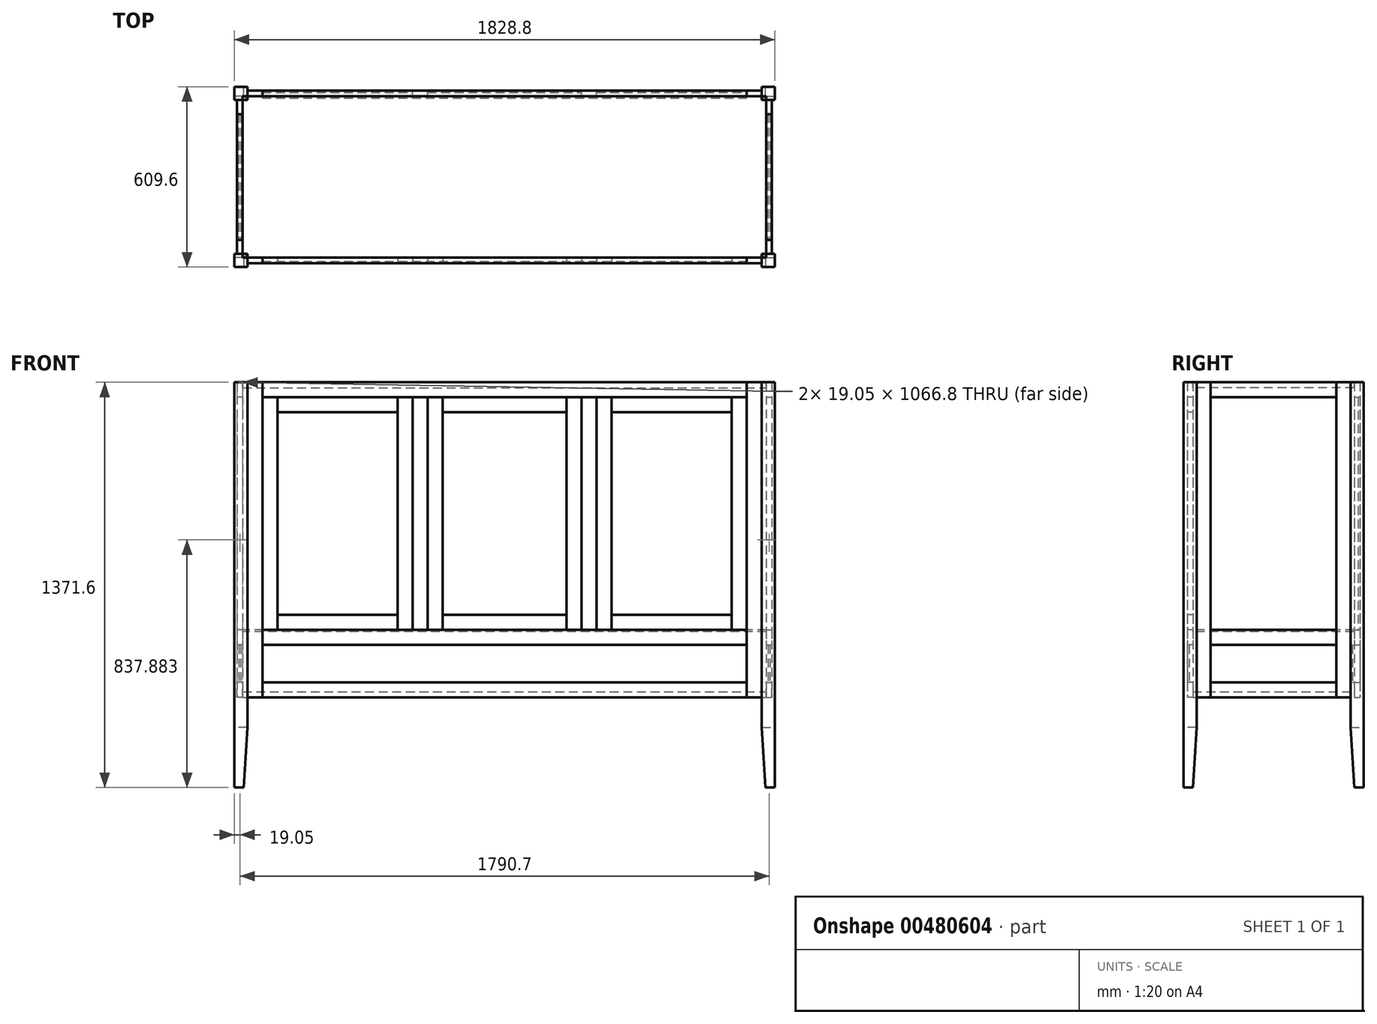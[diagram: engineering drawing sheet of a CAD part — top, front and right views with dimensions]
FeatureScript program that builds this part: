
annotation { "Feature Type Name" : "Feature", "Feature Type Description" : "" }
export const myFeature = defineFeature(function(context is Context, id is Id, definition is map)
    precondition{}
    {
        {
            var Q0;
            Q0=qCreatedBy(makeId("Front.planeOp"),FACE);
            var sketch = newSketch(context, id + "F0", { "sketchPlane" : qUnion([Q0])});
            skLineSegment(sketch, "E0.bottom", {"start": v(-628.95, 1371.6) * mm, "end": v(-584.5, 1371.6) * mm});
            skLineSegment(sketch, "E0.top", {"start": v(-628.95, 0) * mm, "end": v(-584.5, 0) * mm});
            skLineSegment(sketch, "E0.left", {"start": v(-628.95, 1371.6) * mm, "end": v(-628.95, 0) * mm});
            skLineSegment(sketch, "E0.right", {"start": v(-584.5, 1371.6) * mm, "end": v(-584.5, 0) * mm});
            skSolve(sketch);
        }
        {
            var Q0;
            Q0=qSketchRegion(id+"F0",true);
            extrude(context, id + "F1", {"entities" : qUnion([Q0]), "depth" : 44.45 * mm});
        }
        {
            var Q0;
            Q0=makeQuery(id+"F1.opExtrude","CAP_FACE",FACE,{"disambiguationData":[OSD([sQuery(id+"F0.wireOp",EDGE,"E0.bottom"),sQuery(id+"F0.wireOp",EDGE,"E0.top"),sQuery(id+"F0.wireOp",EDGE,"E0.left"),sQuery(id+"F0.wireOp",EDGE,"E0.right")])],"isStart":false});
            var sketch = newSketch(context, id + "F2", { "sketchPlane" : qUnion([Q0])});
            skPoint(sketch, "E1", {"position": v(-584.5, 203.2) * mm});
            skPoint(sketch, "E2", {"position": v(-597.2, 0) * mm});
            skLineSegment(sketch, "E3", {"start": v(-597.2, 0) * mm, "end": v(-584.5, 203.2) * mm});
            skLineSegment(sketch, "E4", {"start": v(-597.2, 0) * mm, "end": v(-584.5, 0) * mm});
            skLineSegment(sketch, "E5", {"start": v(-584.5, 0) * mm, "end": v(-584.5, 203.2) * mm});
            skSolve(sketch);
        }
        {
            var Q0;
            Q0=makeQuery(id+"F2.imprint","IMPRINT",FACE,{"disambiguationData":[TD([[makeQuery(id+"F2.imprint","IMPRINT",EDGE,{"derivedFrom":sQuery(id+"F2.wireOp",EDGE,"E3")}),-1.0]])]});
            extrude(context, id + "F3", {"entities" : qUnion([Q0]), "operationType" : NewBodyOperationType.REMOVE, "endBound" : BoundingType.THROUGH_ALL, "oppositeDirection" : true, "depth" : 25.4 * mm});
        }
        {
            var Q0;
            Q0=makeQuery(id+"F1.opExtrude","SWEPT_FACE",FACE,{"disambiguationData":[OSD([sQuery(id+"F0.wireOp",EDGE,"E0.left")])]});
            var sketch = newSketch(context, id + "F4", { "sketchPlane" : qUnion([Q0])});
            skPoint(sketch, "E6", {"position": v(0, 203.2) * mm});
            skPoint(sketch, "E7", {"position": v(12.7, 0) * mm});
            skLineSegment(sketch, "E8", {"start": v(0, 203.2) * mm, "end": v(12.7, 0) * mm});
            skLineSegment(sketch, "E9", {"start": v(0, 0) * mm, "end": v(0, 203.2) * mm});
            skSolve(sketch);
        }
        {
            var Q0;
            {var subQ0=sQuery(id+"F4.wireOp",EDGE,"E8");Q0=makeQuery(id+"F4.imprint","IMPRINT",FACE,{"disambiguationData":[TD([[makeQuery(id+"F4.imprint","IMPRINT",EDGE,{"derivedFrom":subQ0}),-1.0]])]});}
            extrude(context, id + "F5", {"entities" : qUnion([Q0]), "operationType" : NewBodyOperationType.REMOVE, "endBound" : BoundingType.THROUGH_ALL, "oppositeDirection" : true, "depth" : 25.4 * mm});
        }
        {
            var Q0;
            Q0=makeQuery(id+"F1.opExtrude","CAP_FACE",FACE,{"disambiguationData":[OSD([sQuery(id+"F0.wireOp",EDGE,"E0.bottom"),sQuery(id+"F0.wireOp",EDGE,"E0.top"),sQuery(id+"F0.wireOp",EDGE,"E0.left"),sQuery(id+"F0.wireOp",EDGE,"E0.right")])],"isStart":false});
            cPlane(context, id + "F6", {"entities" : qUnion([Q0]), "cplaneType" : CPlaneType.OFFSET, "offset" : 304.8 * mm, "oppositeDirection" : true, "width" : 152.4 * mm, "height" : 152.4 * mm});
        }
        {
            var Q0;
            Q0=makeQuery(id+"F1.opExtrude","SWEPT_FACE",FACE,{"disambiguationData":[OSD([sQuery(id+"F0.wireOp",EDGE,"E0.left")])]});
            cPlane(context, id + "F7", {"entities" : qUnion([Q0]), "cplaneType" : CPlaneType.OFFSET, "offset" : 9.52 * mm, "oppositeDirection" : true, "width" : 152.4 * mm, "height" : 152.4 * mm});
        }
        {
            var Q0;
            Q0=qCreatedBy(id+"F7.planeOp",FACE);
            var sketch = newSketch(context, id + "F8", { "sketchPlane" : qUnion([Q0])});
            skPoint(sketch, "E10", {"position": v(0, 1371.28) * mm});
            skPoint(sketch, "E11", {"position": v(0, 304.48) * mm});
            skLineSegment(sketch, "E12.bottom", {"start": v(0, 1371.28) * mm, "end": v(-47.62, 1371.28) * mm});
            skLineSegment(sketch, "E12.top", {"start": v(0, 304.48) * mm, "end": v(-47.62, 304.48) * mm});
            skLineSegment(sketch, "E12.left", {"start": v(0, 1371.28) * mm, "end": v(0, 304.48) * mm});
            skLineSegment(sketch, "E12.right", {"start": v(-47.62, 1371.28) * mm, "end": v(-47.62, 304.48) * mm});
            skSolve(sketch);
        }
        {
            var Q0;
            Q0=makeQuery(id+"F8.imprint","IMPRINT",FACE,{"disambiguationData":[TD([[makeQuery(id+"F8.imprint","IMPRINT",EDGE,{"derivedFrom":sQuery(id+"F8.wireOp",EDGE,"E12.bottom")}),1.0]])]});
            extrude(context, id + "F9", {"entities" : qUnion([Q0]), "operationType" : NewBodyOperationType.ADD, "oppositeDirection" : true, "depth" : 19.05 * mm});
        }
        {
            var Q0;
            Q0=makeQuery(id+"F1.opExtrude","SWEPT_BODY",BODY,{"disambiguationData":[OSD([sQuery(id+"F0.wireOp",EDGE,"E0.bottom"),sQuery(id+"F0.wireOp",EDGE,"E0.top"),sQuery(id+"F0.wireOp",EDGE,"E0.left"),sQuery(id+"F0.wireOp",EDGE,"E0.right")])]});
            var Q1;
            Q1=qCreatedBy(id+"F6.planeOp",FACE);
            mirror(context, id + "F10", {"entities" : qUnion([Q0]), "mirrorPlane" : qUnion([Q1])});
        }
        {
            var Q0;
            Q0=qCreatedBy(id+"F7.planeOp",FACE);
            var sketch = newSketch(context, id + "F11", { "sketchPlane" : qUnion([Q0])});
            skLineSegment(sketch, "E13.bottom", {"start": v(-473.08, 1371.28) * mm, "end": v(-47.62, 1371.28) * mm});
            skLineSegment(sketch, "E13.top", {"start": v(-473.08, 1320.48) * mm, "end": v(-47.62, 1320.48) * mm});
            skLineSegment(sketch, "E13.left", {"start": v(-473.08, 1371.28) * mm, "end": v(-473.08, 1320.48) * mm});
            skLineSegment(sketch, "E13.right", {"start": v(-47.62, 1371.28) * mm, "end": v(-47.62, 1320.48) * mm});
            skSolve(sketch);
        }
        {
            var Q0;
            Q0=makeQuery(id+"F11.imprint","IMPRINT",FACE,{"disambiguationData":[TD([[makeQuery(id+"F11.imprint","IMPRINT",EDGE,{"derivedFrom":sQuery(id+"F11.wireOp",EDGE,"E13.bottom")}),-1.0]])]});
            extrude(context, id + "F12", {"entities" : qUnion([Q0]), "oppositeDirection" : true, "depth" : 19.05 * mm});
        }
        {
            var Q0;
            Q0=qCreatedBy(id+"F7.planeOp",FACE);
            var sketch = newSketch(context, id + "F13", { "sketchPlane" : qUnion([Q0])});
            skLineSegment(sketch, "E14.bottom", {"start": v(-473.08, 304.48) * mm, "end": v(-47.62, 304.48) * mm});
            skLineSegment(sketch, "E14.top", {"start": v(-473.08, 355.28) * mm, "end": v(-47.62, 355.28) * mm});
            skLineSegment(sketch, "E14.left", {"start": v(-473.08, 304.48) * mm, "end": v(-473.08, 355.28) * mm});
            skLineSegment(sketch, "E14.right", {"start": v(-47.62, 304.48) * mm, "end": v(-47.62, 355.28) * mm});
            skSolve(sketch);
        }
        {
            var Q0;
            Q0=makeQuery(id+"F13.imprint","IMPRINT",FACE,{"disambiguationData":[TD([[makeQuery(id+"F13.imprint","IMPRINT",EDGE,{"derivedFrom":sQuery(id+"F13.wireOp",EDGE,"E14.bottom")}),1.0]])]});
            extrude(context, id + "F14", {"entities" : qUnion([Q0]), "oppositeDirection" : true, "depth" : 19.05 * mm});
        }
        {
            var Q0;
            Q0=qCreatedBy(id+"F7.planeOp",FACE);
            var sketch = newSketch(context, id + "F15", { "sketchPlane" : qUnion([Q0])});
            skPoint(sketch, "E15", {"position": v(-473.08, 1371.28) * mm});
            skPoint(sketch, "E16", {"position": v(-473.08, 533.08) * mm});
            skLineSegment(sketch, "E17.bottom", {"start": v(-473.08, 533.08) * mm, "end": v(-47.62, 533.08) * mm});
            skLineSegment(sketch, "E17.top", {"start": v(-473.08, 482.28) * mm, "end": v(-47.62, 482.28) * mm});
            skLineSegment(sketch, "E17.left", {"start": v(-473.08, 533.08) * mm, "end": v(-473.08, 482.28) * mm});
            skLineSegment(sketch, "E17.right", {"start": v(-47.62, 533.08) * mm, "end": v(-47.62, 482.28) * mm});
            skSolve(sketch);
        }
        {
            var Q0;
            Q0=makeQuery(id+"F15.imprint","IMPRINT",FACE,{"disambiguationData":[TD([[makeQuery(id+"F15.imprint","IMPRINT",EDGE,{"derivedFrom":sQuery(id+"F15.wireOp",EDGE,"E17.bottom")}),-1.0]])]});
            extrude(context, id + "F16", {"entities" : qUnion([Q0]), "oppositeDirection" : true, "depth" : 19.05 * mm});
        }
        {
            var Q0;
            Q0=makeQuery(id+"F16.opExtrude","CAP_FACE",FACE,{"disambiguationData":[OSD([sQuery(id+"F15.wireOp",EDGE,"E17.bottom"),sQuery(id+"F15.wireOp",EDGE,"E17.top"),sQuery(id+"F15.wireOp",EDGE,"E17.left"),sQuery(id+"F15.wireOp",EDGE,"E17.right")])],"isStart":true});
            cPlane(context, id + "F17", {"entities" : qUnion([Q0]), "cplaneType" : CPlaneType.OFFSET, "offset" : 6.35 * mm, "oppositeDirection" : true, "width" : 152.4 * mm, "height" : 152.4 * mm});
        }
        {
            var Q0;
            Q0=qCreatedBy(id+"F17.planeOp",FACE);
            var sketch = newSketch(context, id + "F18", { "sketchPlane" : qUnion([Q0])});
            skLineSegment(sketch, "E18.bottom", {"start": v(-473.08, 482.28) * mm, "end": v(-47.62, 482.28) * mm});
            skLineSegment(sketch, "E18.top", {"start": v(-473.08, 355.28) * mm, "end": v(-47.62, 355.28) * mm});
            skLineSegment(sketch, "E18.left", {"start": v(-473.08, 482.28) * mm, "end": v(-473.08, 355.28) * mm});
            skLineSegment(sketch, "E18.right", {"start": v(-47.62, 482.28) * mm, "end": v(-47.62, 355.28) * mm});
            skSolve(sketch);
        }
        {
            var Q0;
            Q0=makeQuery(id+"F18.imprint","IMPRINT",FACE,{"disambiguationData":[TD([[makeQuery(id+"F18.imprint","IMPRINT",EDGE,{"derivedFrom":sQuery(id+"F18.wireOp",EDGE,"E18.bottom")}),-1.0]])]});
            extrude(context, id + "F19", {"entities" : qUnion([Q0]), "oppositeDirection" : true, "depth" : 6.35 * mm});
        }
        {
            var Q0;
            Q0=makeQuery(id+"F1.opExtrude","SWEPT_FACE",FACE,{"disambiguationData":[OSD([sQuery(id+"F0.wireOp",EDGE,"E0.left")])]});
            cPlane(context, id + "F20", {"entities" : qUnion([Q0]), "cplaneType" : CPlaneType.OFFSET, "offset" : 914.4 * mm, "oppositeDirection" : true, "width" : 152.4 * mm, "height" : 152.4 * mm});
        }
        {
            var Q0;
            Q0=makeQuery(id+"F1.opExtrude","SWEPT_BODY",BODY,{"disambiguationData":[OSD([sQuery(id+"F0.wireOp",EDGE,"E0.bottom"),sQuery(id+"F0.wireOp",EDGE,"E0.top"),sQuery(id+"F0.wireOp",EDGE,"E0.left"),sQuery(id+"F0.wireOp",EDGE,"E0.right")])]});
            var Q1;
            Q1=makeQuery(id+"F14.opExtrude","SWEPT_BODY",BODY,{"disambiguationData":[OSD([sQuery(id+"F13.wireOp",EDGE,"E14.bottom"),sQuery(id+"F13.wireOp",EDGE,"E14.top"),sQuery(id+"F13.wireOp",EDGE,"E14.left"),sQuery(id+"F13.wireOp",EDGE,"E14.right")])]});
            var Q2;
            Q2=makeQuery(id+"F12.opExtrude","SWEPT_BODY",BODY,{"disambiguationData":[OSD([sQuery(id+"F11.wireOp",EDGE,"E13.bottom"),sQuery(id+"F11.wireOp",EDGE,"E13.top"),sQuery(id+"F11.wireOp",EDGE,"E13.left"),sQuery(id+"F11.wireOp",EDGE,"E13.right")])]});
            var Q3;
            Q3=makeQuery(id+"F10.opPattern","COPY",BODY,{"derivedFrom":makeQuery(id+"F1.opExtrude","SWEPT_BODY",BODY,{"disambiguationData":[OSD([sQuery(id+"F0.wireOp",EDGE,"E0.bottom"),sQuery(id+"F0.wireOp",EDGE,"E0.top"),sQuery(id+"F0.wireOp",EDGE,"E0.left"),sQuery(id+"F0.wireOp",EDGE,"E0.right")])]}),"instanceName":"1"});
            var Q4;
            Q4=makeQuery(id+"F16.opExtrude","SWEPT_BODY",BODY,{"disambiguationData":[OSD([sQuery(id+"F15.wireOp",EDGE,"E17.bottom"),sQuery(id+"F15.wireOp",EDGE,"E17.top"),sQuery(id+"F15.wireOp",EDGE,"E17.left"),sQuery(id+"F15.wireOp",EDGE,"E17.right")])]});
            var Q5;
            Q5=makeQuery(id+"F19.opExtrude","SWEPT_BODY",BODY,{"disambiguationData":[OSD([sQuery(id+"F18.wireOp",EDGE,"E18.bottom"),sQuery(id+"F18.wireOp",EDGE,"E18.top"),sQuery(id+"F18.wireOp",EDGE,"E18.left"),sQuery(id+"F18.wireOp",EDGE,"E18.right")])]});
            var Q6;
            Q6=qCreatedBy(id+"F20.planeOp",FACE);
            mirror(context, id + "F21", {"entities" : qUnion([Q0, Q1, Q2, Q3, Q4, Q5]), "mirrorPlane" : qUnion([Q6])});
        }
        {
            var Q0;
            Q0=makeQuery(id+"F21.opPattern","COPY",FACE,{"derivedFrom":makeQuery(id+"F1.opExtrude","CAP_FACE",FACE,{"disambiguationData":[OSD([sQuery(id+"F0.wireOp",EDGE,"E0.bottom"),sQuery(id+"F0.wireOp",EDGE,"E0.top"),sQuery(id+"F0.wireOp",EDGE,"E0.left"),sQuery(id+"F0.wireOp",EDGE,"E0.right")])],"isStart":false}),"instanceName":"1"});
            cPlane(context, id + "F22", {"entities" : qUnion([Q0]), "cplaneType" : CPlaneType.OFFSET, "offset" : 12.7 * mm, "oppositeDirection" : true, "width" : 152.4 * mm, "height" : 152.4 * mm});
        }
        {
            var Q0;
            Q0=qCreatedBy(id+"F22.planeOp",FACE);
            var sketch = newSketch(context, id + "F23", { "sketchPlane" : qUnion([Q0])});
            skLineSegment(sketch, "E19.bottom", {"start": v(-584.5, 1371.6) * mm, "end": v(-533.7, 1371.6) * mm});
            skLineSegment(sketch, "E19.top", {"start": v(-584.5, 304.48) * mm, "end": v(-533.7, 304.48) * mm});
            skLineSegment(sketch, "E19.left", {"start": v(-584.5, 1371.6) * mm, "end": v(-584.5, 304.48) * mm});
            skLineSegment(sketch, "E19.right", {"start": v(-533.7, 1371.6) * mm, "end": v(-533.7, 304.48) * mm});
            skSolve(sketch);
        }
        {
            var Q0;
            Q0=qSketchRegion(id+"F23",true);
            extrude(context, id + "F24", {"entities" : qUnion([Q0]), "oppositeDirection" : true, "depth" : 19.05 * mm});
        }
        {
            var Q0;
            Q0=qCreatedBy(id+"F22.planeOp",FACE);
            var sketch = newSketch(context, id + "F25", { "sketchPlane" : qUnion([Q0])});
            skLineSegment(sketch, "E20.bottom", {"start": v(-533.7, 1371.6) * mm, "end": v(1104.6, 1371.6) * mm});
            skLineSegment(sketch, "E20.top", {"start": v(-533.7, 1320.8) * mm, "end": v(1104.6, 1320.8) * mm});
            skLineSegment(sketch, "E20.left", {"start": v(-533.7, 1371.6) * mm, "end": v(-533.7, 1320.8) * mm});
            skLineSegment(sketch, "E20.right", {"start": v(1104.6, 1371.6) * mm, "end": v(1104.6, 1320.8) * mm});
            skSolve(sketch);
        }
        {
            var Q0;
            Q0=qSketchRegion(id+"F25",true);
            extrude(context, id + "F26", {"entities" : qUnion([Q0]), "oppositeDirection" : true, "depth" : 19.05 * mm});
        }
        {
            var Q0;
            Q0=makeQuery(id+"F24.opExtrude","SWEPT_BODY",BODY,{"disambiguationData":[OSD([sQuery(id+"F23.wireOp",EDGE,"E19.bottom"),sQuery(id+"F23.wireOp",EDGE,"E19.top"),sQuery(id+"F23.wireOp",EDGE,"E19.left"),sQuery(id+"F23.wireOp",EDGE,"E19.right")])]});
            var Q1;
            Q1=qCreatedBy(id+"F20.planeOp",FACE);
            mirror(context, id + "F27", {"entities" : qUnion([Q0]), "mirrorPlane" : qUnion([Q1])});
        }
        {
            var Q0;
            Q0=qCreatedBy(id+"F22.planeOp",FACE);
            var sketch = newSketch(context, id + "F28", { "sketchPlane" : qUnion([Q0])});
            skLineSegment(sketch, "E21.bottom", {"start": v(-533.7, 355.28) * mm, "end": v(1104.6, 355.28) * mm});
            skLineSegment(sketch, "E21.top", {"start": v(-533.7, 304.48) * mm, "end": v(1104.6, 304.48) * mm});
            skLineSegment(sketch, "E21.left", {"start": v(-533.7, 355.28) * mm, "end": v(-533.7, 304.48) * mm});
            skLineSegment(sketch, "E21.right", {"start": v(1104.6, 355.28) * mm, "end": v(1104.6, 304.48) * mm});
            skSolve(sketch);
        }
        {
            var Q0;
            Q0=qSketchRegion(id+"F28",true);
            extrude(context, id + "F29", {"entities" : qUnion([Q0]), "oppositeDirection" : true, "depth" : 19.05 * mm});
        }
        {
            var Q0;
            Q0=qCreatedBy(id+"F22.planeOp",FACE);
            var sketch = newSketch(context, id + "F30", { "sketchPlane" : qUnion([Q0])});
            skLineSegment(sketch, "E22.bottom", {"start": v(-533.7, 533.08) * mm, "end": v(1104.6, 533.08) * mm});
            skLineSegment(sketch, "E22.top", {"start": v(-533.7, 482.28) * mm, "end": v(1104.6, 482.28) * mm});
            skLineSegment(sketch, "E22.left", {"start": v(-533.7, 533.08) * mm, "end": v(-533.7, 482.28) * mm});
            skLineSegment(sketch, "E22.right", {"start": v(1104.6, 533.08) * mm, "end": v(1104.6, 482.28) * mm});
            skSolve(sketch);
        }
        {
            var Q0;
            Q0=qSketchRegion(id+"F30",true);
            extrude(context, id + "F31", {"entities" : qUnion([Q0]), "oppositeDirection" : true, "depth" : 19.05 * mm});
        }
        {
            var Q0;
            Q0=qCreatedBy(id+"F22.planeOp",FACE);
            var sketch = newSketch(context, id + "F32", { "sketchPlane" : qUnion([Q0])});
            skLineSegment(sketch, "E23.bottom", {"start": v(-25.7, 1320.8) * mm, "end": v(25.1, 1320.8) * mm});
            skLineSegment(sketch, "E23.top", {"start": v(-25.7, 533.08) * mm, "end": v(25.1, 533.08) * mm});
            skLineSegment(sketch, "E23.left", {"start": v(-25.7, 1320.8) * mm, "end": v(-25.7, 533.08) * mm});
            skLineSegment(sketch, "E23.right", {"start": v(25.1, 1320.8) * mm, "end": v(25.1, 533.08) * mm});
            skSolve(sketch);
        }
        {
            var Q0;
            Q0=qSketchRegion(id+"F32",true);
            extrude(context, id + "F33", {"entities" : qUnion([Q0]), "oppositeDirection" : true, "depth" : 19.05 * mm});
        }
        {
            var Q0;
            Q0=makeQuery(id+"F33.opExtrude","SWEPT_BODY",BODY,{"disambiguationData":[OSD([sQuery(id+"F32.wireOp",EDGE,"E23.bottom"),sQuery(id+"F32.wireOp",EDGE,"E23.top"),sQuery(id+"F32.wireOp",EDGE,"E23.left"),sQuery(id+"F32.wireOp",EDGE,"E23.right")])]});
            var Q1;
            Q1=makeQuery(id+"FRYgR2zi93UsPrp_9.opExtrude","SWEPT_BODY",BODY,{"disambiguationData":[OSD([sQuery(id+"FfaSuB3CfZjcmVR_9.wireOp",EDGE,"jGVs514A-PyTt-ZbNQ-JDFk-VF9dIN6a2kFS.bottom"),sQuery(id+"FfaSuB3CfZjcmVR_9.wireOp",EDGE,"jGVs514A-PyTt-ZbNQ-JDFk-VF9dIN6a2kFS.top"),sQuery(id+"FfaSuB3CfZjcmVR_9.wireOp",EDGE,"jGVs514A-PyTt-ZbNQ-JDFk-VF9dIN6a2kFS.left"),sQuery(id+"FfaSuB3CfZjcmVR_9.wireOp",EDGE,"jGVs514A-PyTt-ZbNQ-JDFk-VF9dIN6a2kFS.right")])]});
            var Q2;
            Q2=qCreatedBy(id+"F20.planeOp",FACE);
            mirror(context, id + "F34", {"entities" : qUnion([Q0, Q1]), "mirrorPlane" : qUnion([Q2])});
        }
        {
            var Q0;
            Q0=makeQuery(id+"F24.opExtrude","SWEPT_BODY",BODY,{"disambiguationData":[OSD([sQuery(id+"F23.wireOp",EDGE,"E19.bottom"),sQuery(id+"F23.wireOp",EDGE,"E19.top"),sQuery(id+"F23.wireOp",EDGE,"E19.left"),sQuery(id+"F23.wireOp",EDGE,"E19.right")])]});
            var Q1;
            Q1=makeQuery(id+"F26.opExtrude","SWEPT_BODY",BODY,{"disambiguationData":[OSD([sQuery(id+"F25.wireOp",EDGE,"E20.bottom"),sQuery(id+"F25.wireOp",EDGE,"E20.top"),sQuery(id+"F25.wireOp",EDGE,"E20.left"),sQuery(id+"F25.wireOp",EDGE,"E20.right")])]});
            var Q2;
            Q2=makeQuery(id+"F33.opExtrude","SWEPT_BODY",BODY,{"disambiguationData":[OSD([sQuery(id+"F32.wireOp",EDGE,"E23.bottom"),sQuery(id+"F32.wireOp",EDGE,"E23.top"),sQuery(id+"F32.wireOp",EDGE,"E23.left"),sQuery(id+"F32.wireOp",EDGE,"E23.right")])]});
            var Q3;
            Q3=makeQuery(id+"F34.opPattern","COPY",BODY,{"derivedFrom":makeQuery(id+"F33.opExtrude","SWEPT_BODY",BODY,{"disambiguationData":[OSD([sQuery(id+"F32.wireOp",EDGE,"E23.bottom"),sQuery(id+"F32.wireOp",EDGE,"E23.top"),sQuery(id+"F32.wireOp",EDGE,"E23.left"),sQuery(id+"F32.wireOp",EDGE,"E23.right")])]}),"instanceName":"1"});
            var Q4;
            Q4=makeQuery(id+"F27.opPattern","COPY",BODY,{"derivedFrom":makeQuery(id+"F24.opExtrude","SWEPT_BODY",BODY,{"disambiguationData":[OSD([sQuery(id+"F23.wireOp",EDGE,"E19.bottom"),sQuery(id+"F23.wireOp",EDGE,"E19.top"),sQuery(id+"F23.wireOp",EDGE,"E19.left"),sQuery(id+"F23.wireOp",EDGE,"E19.right")])]}),"instanceName":"1"});
            var Q5;
            Q5=makeQuery(id+"F31.opExtrude","SWEPT_BODY",BODY,{"disambiguationData":[OSD([sQuery(id+"F30.wireOp",EDGE,"E22.bottom"),sQuery(id+"F30.wireOp",EDGE,"E22.top"),sQuery(id+"F30.wireOp",EDGE,"E22.left"),sQuery(id+"F30.wireOp",EDGE,"E22.right")])]});
            var Q6;
            Q6=makeQuery(id+"F29.opExtrude","SWEPT_BODY",BODY,{"disambiguationData":[OSD([sQuery(id+"F28.wireOp",EDGE,"E21.bottom"),sQuery(id+"F28.wireOp",EDGE,"E21.top"),sQuery(id+"F28.wireOp",EDGE,"E21.left"),sQuery(id+"F28.wireOp",EDGE,"E21.right")])]});
            var Q7;
            Q7=makeQuery(id+"F34.opPattern","COPY",BODY,{"derivedFrom":makeQuery(id+"FRYgR2zi93UsPrp_9.opExtrude","SWEPT_BODY",BODY,{"disambiguationData":[OSD([sQuery(id+"FfaSuB3CfZjcmVR_9.wireOp",EDGE,"jGVs514A-PyTt-ZbNQ-JDFk-VF9dIN6a2kFS.bottom"),sQuery(id+"FfaSuB3CfZjcmVR_9.wireOp",EDGE,"jGVs514A-PyTt-ZbNQ-JDFk-VF9dIN6a2kFS.top"),sQuery(id+"FfaSuB3CfZjcmVR_9.wireOp",EDGE,"jGVs514A-PyTt-ZbNQ-JDFk-VF9dIN6a2kFS.left"),sQuery(id+"FfaSuB3CfZjcmVR_9.wireOp",EDGE,"jGVs514A-PyTt-ZbNQ-JDFk-VF9dIN6a2kFS.right")])]}),"instanceName":"1"});
            var Q8;
            Q8=makeQuery(id+"FRYgR2zi93UsPrp_9.opExtrude","SWEPT_BODY",BODY,{"disambiguationData":[OSD([sQuery(id+"FfaSuB3CfZjcmVR_9.wireOp",EDGE,"jGVs514A-PyTt-ZbNQ-JDFk-VF9dIN6a2kFS.bottom"),sQuery(id+"FfaSuB3CfZjcmVR_9.wireOp",EDGE,"jGVs514A-PyTt-ZbNQ-JDFk-VF9dIN6a2kFS.top"),sQuery(id+"FfaSuB3CfZjcmVR_9.wireOp",EDGE,"jGVs514A-PyTt-ZbNQ-JDFk-VF9dIN6a2kFS.left"),sQuery(id+"FfaSuB3CfZjcmVR_9.wireOp",EDGE,"jGVs514A-PyTt-ZbNQ-JDFk-VF9dIN6a2kFS.right")])]});
            var Q9;
            Q9=makeQuery(id+"FIeeD6PPRITTbVt_10.opExtrude","SWEPT_BODY",BODY,{"disambiguationData":[OSD([sQuery(id+"FnYbJkNIQu2NAMf_10.wireOp",EDGE,"rAF0CF05-2Poy-62uF-igAy-b5mA2g4RPxVq.bottom"),sQuery(id+"FnYbJkNIQu2NAMf_10.wireOp",EDGE,"rAF0CF05-2Poy-62uF-igAy-b5mA2g4RPxVq.top"),sQuery(id+"FnYbJkNIQu2NAMf_10.wireOp",EDGE,"rAF0CF05-2Poy-62uF-igAy-b5mA2g4RPxVq.left"),sQuery(id+"FnYbJkNIQu2NAMf_10.wireOp",EDGE,"rAF0CF05-2Poy-62uF-igAy-b5mA2g4RPxVq.right")])]});
            var Q10;
            Q10=makeQuery(id+"FIeeD6PPRITTbVt_10.opExtrude","SWEPT_BODY",BODY,{"disambiguationData":[OSD([sQuery(id+"FnYbJkNIQu2NAMf_10.wireOp",EDGE,"fFBXAJHD-Mimp-aTbj-Gqx7-02bonivjZSQP.bottom"),sQuery(id+"FnYbJkNIQu2NAMf_10.wireOp",EDGE,"fFBXAJHD-Mimp-aTbj-Gqx7-02bonivjZSQP.top"),sQuery(id+"FnYbJkNIQu2NAMf_10.wireOp",EDGE,"fFBXAJHD-Mimp-aTbj-Gqx7-02bonivjZSQP.left"),sQuery(id+"FnYbJkNIQu2NAMf_10.wireOp",EDGE,"fFBXAJHD-Mimp-aTbj-Gqx7-02bonivjZSQP.right")])]});
            var Q11;
            Q11=makeQuery(id+"FIeeD6PPRITTbVt_10.opExtrude","SWEPT_BODY",BODY,{"disambiguationData":[OSD([sQuery(id+"FnYbJkNIQu2NAMf_10.wireOp",EDGE,"xDAJZFGa-3O6M-nzbW-7IkL-r6EZniyfeXkM.bottom"),sQuery(id+"FnYbJkNIQu2NAMf_10.wireOp",EDGE,"xDAJZFGa-3O6M-nzbW-7IkL-r6EZniyfeXkM.top"),sQuery(id+"FnYbJkNIQu2NAMf_10.wireOp",EDGE,"xDAJZFGa-3O6M-nzbW-7IkL-r6EZniyfeXkM.left"),sQuery(id+"FnYbJkNIQu2NAMf_10.wireOp",EDGE,"xDAJZFGa-3O6M-nzbW-7IkL-r6EZniyfeXkM.right")])]});
            var Q12;
            Q12=qCreatedBy(id+"F6.planeOp",FACE);
            mirror(context, id + "F35", {"entities" : qUnion([Q0, Q1, Q2, Q3, Q4, Q5, Q6, Q7, Q8, Q9, Q10, Q11]), "mirrorPlane" : qUnion([Q12])});
        }
        {
            var Q0;
            Q0=qCreatedBy(id+"F22.planeOp",FACE);
            var sketch = newSketch(context, id + "F36", { "sketchPlane" : qUnion([Q0])});
            skLineSegment(sketch, "E24.bottom", {"start": v(-533.7, 1320.8) * mm, "end": v(-482.9, 1320.8) * mm});
            skLineSegment(sketch, "E24.top", {"start": v(-533.7, 533.08) * mm, "end": v(-482.9, 533.08) * mm});
            skLineSegment(sketch, "E24.left", {"start": v(-533.7, 1320.8) * mm, "end": v(-533.7, 533.08) * mm});
            skLineSegment(sketch, "E24.right", {"start": v(-482.9, 1320.8) * mm, "end": v(-482.9, 533.08) * mm});
            skSolve(sketch);
        }
        {
            var Q0;
            Q0=qSketchRegion(id+"F36",true);
            extrude(context, id + "F37", {"entities" : qUnion([Q0]), "oppositeDirection" : true, "depth" : 19.05 * mm});
        }
        {
            var Q0;
            Q0=qCreatedBy(id+"F22.planeOp",FACE);
            var sketch = newSketch(context, id + "F38", { "sketchPlane" : qUnion([Q0])});
            skLineSegment(sketch, "E25.bottom", {"start": v(-76.5, 1320.8) * mm, "end": v(-25.7, 1320.8) * mm});
            skLineSegment(sketch, "E25.top", {"start": v(-76.5, 533.08) * mm, "end": v(-25.7, 533.08) * mm});
            skLineSegment(sketch, "E25.left", {"start": v(-76.5, 1320.8) * mm, "end": v(-76.5, 533.08) * mm});
            skLineSegment(sketch, "E25.right", {"start": v(-25.7, 1320.8) * mm, "end": v(-25.7, 533.08) * mm});
            skSolve(sketch);
        }
        {
            var Q0;
            Q0=qSketchRegion(id+"F38",true);
            extrude(context, id + "F39", {"entities" : qUnion([Q0]), "oppositeDirection" : true, "depth" : 19.05 * mm});
        }
        {
            var Q0;
            Q0=qCreatedBy(id+"F22.planeOp",FACE);
            var sketch = newSketch(context, id + "F40", { "sketchPlane" : qUnion([Q0])});
            skLineSegment(sketch, "E26.bottom", {"start": v(-482.9, 1320.8) * mm, "end": v(-76.5, 1320.8) * mm});
            skLineSegment(sketch, "E26.top", {"start": v(-482.9, 1270) * mm, "end": v(-76.5, 1270) * mm});
            skLineSegment(sketch, "E26.left", {"start": v(-482.9, 1320.8) * mm, "end": v(-482.9, 1270) * mm});
            skLineSegment(sketch, "E26.right", {"start": v(-76.5, 1320.8) * mm, "end": v(-76.5, 1270) * mm});
            skSolve(sketch);
        }
        {
            var Q0;
            Q0=qSketchRegion(id+"F40",true);
            extrude(context, id + "F41", {"entities" : qUnion([Q0]), "oppositeDirection" : true, "depth" : 19.05 * mm});
        }
        {
            var Q0;
            Q0=qCreatedBy(id+"F22.planeOp",FACE);
            var sketch = newSketch(context, id + "F42", { "sketchPlane" : qUnion([Q0])});
            skLineSegment(sketch, "E27.bottom", {"start": v(-482.9, 583.88) * mm, "end": v(-76.5, 583.88) * mm});
            skLineSegment(sketch, "E27.top", {"start": v(-482.9, 533.08) * mm, "end": v(-76.5, 533.08) * mm});
            skLineSegment(sketch, "E27.left", {"start": v(-482.9, 583.88) * mm, "end": v(-482.9, 533.08) * mm});
            skLineSegment(sketch, "E27.right", {"start": v(-76.5, 583.88) * mm, "end": v(-76.5, 533.08) * mm});
            skSolve(sketch);
        }
        {
            var Q0;
            Q0=qSketchRegion(id+"F42",true);
            extrude(context, id + "F43", {"entities" : qUnion([Q0]), "oppositeDirection" : true, "depth" : 19.05 * mm});
        }
        {
            var Q0;
            Q0=makeQuery(id+"F37.opExtrude","SWEPT_BODY",BODY,{"disambiguationData":[OSD([sQuery(id+"F36.wireOp",EDGE,"E24.bottom"),sQuery(id+"F36.wireOp",EDGE,"E24.top"),sQuery(id+"F36.wireOp",EDGE,"E24.left"),sQuery(id+"F36.wireOp",EDGE,"E24.right")])]});
            var Q1;
            Q1=makeQuery(id+"F41.opExtrude","SWEPT_BODY",BODY,{"disambiguationData":[OSD([sQuery(id+"F40.wireOp",EDGE,"E26.bottom"),sQuery(id+"F40.wireOp",EDGE,"E26.top"),sQuery(id+"F40.wireOp",EDGE,"E26.left"),sQuery(id+"F40.wireOp",EDGE,"E26.right")])]});
            var Q2;
            Q2=makeQuery(id+"F39.opExtrude","SWEPT_BODY",BODY,{"disambiguationData":[OSD([sQuery(id+"F38.wireOp",EDGE,"E25.bottom"),sQuery(id+"F38.wireOp",EDGE,"E25.top"),sQuery(id+"F38.wireOp",EDGE,"E25.left"),sQuery(id+"F38.wireOp",EDGE,"E25.right")])]});
            var Q3;
            Q3=makeQuery(id+"F43.opExtrude","SWEPT_BODY",BODY,{"disambiguationData":[OSD([sQuery(id+"F42.wireOp",EDGE,"E27.bottom"),sQuery(id+"F42.wireOp",EDGE,"E27.top"),sQuery(id+"F42.wireOp",EDGE,"E27.left"),sQuery(id+"F42.wireOp",EDGE,"E27.right")])]});
            var Q4;
            Q4=qCreatedBy(id+"F20.planeOp",FACE);
            mirror(context, id + "F44", {"entities" : qUnion([Q0, Q1, Q2, Q3]), "mirrorPlane" : qUnion([Q4])});
        }
        {
            var Q0;
            Q0=qCreatedBy(id+"F22.planeOp",FACE);
            var sketch = newSketch(context, id + "F45", { "sketchPlane" : qUnion([Q0])});
            skLineSegment(sketch, "E28.bottom", {"start": v(25.1, 1320.8) * mm, "end": v(75.9, 1320.8) * mm});
            skLineSegment(sketch, "E28.top", {"start": v(25.1, 533.08) * mm, "end": v(75.9, 533.08) * mm});
            skLineSegment(sketch, "E28.left", {"start": v(25.1, 1320.8) * mm, "end": v(25.1, 533.08) * mm});
            skLineSegment(sketch, "E28.right", {"start": v(75.9, 1320.8) * mm, "end": v(75.9, 533.08) * mm});
            skSolve(sketch);
        }
        {
            var Q0;
            Q0=qSketchRegion(id+"F45",true);
            extrude(context, id + "F46", {"entities" : qUnion([Q0]), "oppositeDirection" : true, "depth" : 19.05 * mm});
        }
        {
            var Q0;
            Q0=qCreatedBy(id+"F22.planeOp",FACE);
            var sketch = newSketch(context, id + "F47", { "sketchPlane" : qUnion([Q0])});
            skLineSegment(sketch, "E29.bottom", {"start": v(495, 1320.8) * mm, "end": v(545.8, 1320.8) * mm});
            skLineSegment(sketch, "E29.top", {"start": v(495, 533.08) * mm, "end": v(545.8, 533.08) * mm});
            skLineSegment(sketch, "E29.left", {"start": v(495, 1320.8) * mm, "end": v(495, 533.08) * mm});
            skLineSegment(sketch, "E29.right", {"start": v(545.8, 1320.8) * mm, "end": v(545.8, 533.08) * mm});
            skSolve(sketch);
        }
        {
            var Q0;
            Q0=qSketchRegion(id+"F47",true);
            extrude(context, id + "F48", {"entities" : qUnion([Q0]), "oppositeDirection" : true, "depth" : 19.05 * mm});
        }
        {
            var Q0;
            Q0=qCreatedBy(id+"F22.planeOp",FACE);
            var sketch = newSketch(context, id + "F49", { "sketchPlane" : qUnion([Q0])});
            skLineSegment(sketch, "E30.bottom", {"start": v(75.9, 1320.8) * mm, "end": v(495, 1320.8) * mm});
            skLineSegment(sketch, "E30.top", {"start": v(75.9, 1270) * mm, "end": v(495, 1270) * mm});
            skLineSegment(sketch, "E30.left", {"start": v(75.9, 1320.8) * mm, "end": v(75.9, 1270) * mm});
            skLineSegment(sketch, "E30.right", {"start": v(495, 1320.8) * mm, "end": v(495, 1270) * mm});
            skSolve(sketch);
        }
        {
            var Q0;
            Q0=qSketchRegion(id+"F49",true);
            extrude(context, id + "F50", {"entities" : qUnion([Q0]), "oppositeDirection" : true, "depth" : 19.05 * mm});
        }
        {
            var Q0;
            Q0=qCreatedBy(id+"F22.planeOp",FACE);
            var sketch = newSketch(context, id + "F51", { "sketchPlane" : qUnion([Q0])});
            skLineSegment(sketch, "E31.bottom", {"start": v(75.9, 583.88) * mm, "end": v(495, 583.88) * mm});
            skLineSegment(sketch, "E31.top", {"start": v(75.9, 533.08) * mm, "end": v(495, 533.08) * mm});
            skLineSegment(sketch, "E31.left", {"start": v(75.9, 583.88) * mm, "end": v(75.9, 533.08) * mm});
            skLineSegment(sketch, "E31.right", {"start": v(495, 583.88) * mm, "end": v(495, 533.08) * mm});
            skSolve(sketch);
        }
        {
            var Q0;
            Q0=qSketchRegion(id+"F51",true);
            extrude(context, id + "F52", {"entities" : qUnion([Q0]), "oppositeDirection" : true, "depth" : 19.05 * mm});
        }
        {
            var Q0;
            Q0=makeQuery(id+"F10.opPattern","COPY",FACE,{"derivedFrom":makeQuery(id+"F1.opExtrude","SWEPT_FACE",FACE,{"disambiguationData":[OSD([sQuery(id+"F0.wireOp",EDGE,"E0.bottom")])]}),"instanceName":"1"});
            var sketch = newSketch(context, id + "F53", { "sketchPlane" : qUnion([Q0])});
            skLineSegment(sketch, "E32.bottom", {"start": v(-600.37, 533.4) * mm, "end": v(1171.28, 533.4) * mm});
            skLineSegment(sketch, "E32.top", {"start": v(-600.37, -12.7) * mm, "end": v(1171.28, -12.7) * mm});
            skLineSegment(sketch, "E32.left", {"start": v(-600.37, 533.4) * mm, "end": v(-600.37, -12.7) * mm});
            skLineSegment(sketch, "E32.right", {"start": v(1171.28, 533.4) * mm, "end": v(1171.28, -12.7) * mm});
            skSolve(sketch);
        }
        {
            var Q0;
            Q0=qSketchRegion(id+"F53",true);
            extrude(context, id + "F54", {"entities" : qUnion([Q0]), "oppositeDirection" : true, "depth" : 19.05 * mm});
        }
        {
            var Q0;
            Q0=makeQuery(id+"F29.opExtrude","SWEPT_FACE",FACE,{"disambiguationData":[OSD([sQuery(id+"F28.wireOp",EDGE,"E21.top")])]});
            var sketch = newSketch(context, id + "F55", { "sketchPlane" : qUnion([Q0])});
            skLineSegment(sketch, "E33.bottom", {"start": v(-600.37, 12.7) * mm, "end": v(1171.28, 12.7) * mm});
            skLineSegment(sketch, "E33.top", {"start": v(-600.37, -533.4) * mm, "end": v(1171.28, -533.4) * mm});
            skLineSegment(sketch, "E33.left", {"start": v(-600.37, 12.7) * mm, "end": v(-600.37, -533.4) * mm});
            skLineSegment(sketch, "E33.right", {"start": v(1171.28, 12.7) * mm, "end": v(1171.28, -533.4) * mm});
            skSolve(sketch);
        }
        {
            var Q0;
            Q0=qSketchRegion(id+"F55",true);
            extrude(context, id + "F56", {"entities" : qUnion([Q0]), "oppositeDirection" : true, "depth" : 19.05 * mm});
        }
        {
            var Q0;
            Q0=makeQuery(id+"F31.opExtrude","CAP_FACE",FACE,{"disambiguationData":[OSD([sQuery(id+"F30.wireOp",EDGE,"E22.bottom"),sQuery(id+"F30.wireOp",EDGE,"E22.top"),sQuery(id+"F30.wireOp",EDGE,"E22.left"),sQuery(id+"F30.wireOp",EDGE,"E22.right")])],"isStart":true});
            var sketch = newSketch(context, id + "F57", { "sketchPlane" : qUnion([Q0])});
            skLineSegment(sketch, "E34.bottom", {"start": v(-533.7, 482.28) * mm, "end": v(1104.6, 482.28) * mm});
            skLineSegment(sketch, "E34.top", {"start": v(-533.7, 355.28) * mm, "end": v(1104.6, 355.28) * mm});
            skLineSegment(sketch, "E34.left", {"start": v(-533.7, 482.28) * mm, "end": v(-533.7, 355.28) * mm});
            skLineSegment(sketch, "E34.right", {"start": v(1104.6, 482.28) * mm, "end": v(1104.6, 355.28) * mm});
            skSolve(sketch);
        }
        {
            var Q0;
            Q0 = qSketchRegion(id + "F57", true);
            extrude(context, id + "F58", {"entities" : qUnion([Q0]), "oppositeDirection" : true, "depth" : 6.35 * mm});
        }
        {
            var Q0;
            Q0=makeQuery(id+"F35.opPattern","COPY",FACE,{"derivedFrom":makeQuery(id+"F31.opExtrude","CAP_FACE",FACE,{"disambiguationData":[OSD([sQuery(id+"F30.wireOp",EDGE,"E22.bottom"),sQuery(id+"F30.wireOp",EDGE,"E22.top"),sQuery(id+"F30.wireOp",EDGE,"E22.left"),sQuery(id+"F30.wireOp",EDGE,"E22.right")])],"isStart":true}),"instanceName":"1"});
            var sketch = newSketch(context, id + "F59", { "sketchPlane" : qUnion([Q0])});
            skLineSegment(sketch, "E35.bottom", {"start": v(-1104.6, 482.28) * mm, "end": v(533.7, 482.28) * mm});
            skLineSegment(sketch, "E35.top", {"start": v(-1104.6, 355.28) * mm, "end": v(533.7, 355.28) * mm});
            skLineSegment(sketch, "E35.left", {"start": v(-1104.6, 482.28) * mm, "end": v(-1104.6, 355.28) * mm});
            skLineSegment(sketch, "E35.right", {"start": v(533.7, 482.28) * mm, "end": v(533.7, 355.28) * mm});
            skSolve(sketch);
        }
        {
            var Q0;
            Q0 = qSketchRegion(id + "F59", true);
            extrude(context, id + "F60", {"entities" : qUnion([Q0]), "oppositeDirection" : true, "depth" : 25.4 * mm});
        }
        {
            var Q0;
            Q0=makeQuery(id+"F35.opPattern","COPY",FACE,{"derivedFrom":makeQuery(id+"F26.opExtrude","CAP_FACE",FACE,{"disambiguationData":[OSD([sQuery(id+"F25.wireOp",EDGE,"E20.bottom"),sQuery(id+"F25.wireOp",EDGE,"E20.top"),sQuery(id+"F25.wireOp",EDGE,"E20.left"),sQuery(id+"F25.wireOp",EDGE,"E20.right")])],"isStart":true}),"instanceName":"1"});
            var sketch = newSketch(context, id + "F61", { "sketchPlane" : qUnion([Q0])});
            skLineSegment(sketch, "E36.bottom", {"start": v(-1104.6, 1320.8) * mm, "end": v(-596.6, 1320.8) * mm});
            skLineSegment(sketch, "E36.top", {"start": v(-1104.6, 533.08) * mm, "end": v(-596.6, 533.08) * mm});
            skLineSegment(sketch, "E36.left", {"start": v(-1104.6, 1320.8) * mm, "end": v(-1104.6, 533.08) * mm});
            skLineSegment(sketch, "E36.right", {"start": v(-596.6, 1320.8) * mm, "end": v(-596.6, 533.08) * mm});
            skLineSegment(sketch, "E37.bottom", {"start": v(-545.8, 1320.8) * mm, "end": v(-25.1, 1320.8) * mm});
            skLineSegment(sketch, "E37.top", {"start": v(-545.8, 533.08) * mm, "end": v(-25.1, 533.08) * mm});
            skLineSegment(sketch, "E37.left", {"start": v(-545.8, 1320.8) * mm, "end": v(-545.8, 533.08) * mm});
            skLineSegment(sketch, "E37.right", {"start": v(-25.1, 1320.8) * mm, "end": v(-25.1, 533.08) * mm});
            skLineSegment(sketch, "E38.bottom", {"start": v(25.7, 1320.8) * mm, "end": v(533.7, 1320.8) * mm});
            skLineSegment(sketch, "E38.top", {"start": v(25.7, 533.08) * mm, "end": v(533.7, 533.08) * mm});
            skLineSegment(sketch, "E38.left", {"start": v(25.7, 1320.8) * mm, "end": v(25.7, 533.08) * mm});
            skLineSegment(sketch, "E38.right", {"start": v(533.7, 1320.8) * mm, "end": v(533.7, 533.08) * mm});
            skSolve(sketch);
        }
        {
            var Q0;
            Q0 = qSketchRegion(id + "F61", true);
            extrude(context, id + "F62", {"entities" : qUnion([Q0]), "oppositeDirection" : true, "depth" : 6.35 * mm});
        }
        {
            var Q0;
            Q0=makeQuery(id+"F35.opPattern","COPY",FACE,{"derivedFrom":makeQuery(id+"F31.opExtrude","SWEPT_FACE",FACE,{"disambiguationData":[OSD([sQuery(id+"F30.wireOp",EDGE,"E22.bottom")])]}),"instanceName":"1"});
            var sketch = newSketch(context, id + "F63", { "sketchPlane" : qUnion([Q0])});
            skLineSegment(sketch, "E39.bottom", {"start": v(1171.28, 533.4) * mm, "end": v(-600.37, 533.4) * mm});
            skLineSegment(sketch, "E39.top", {"start": v(1171.28, -12.7) * mm, "end": v(-600.37, -12.7) * mm});
            skLineSegment(sketch, "E39.left", {"start": v(1171.28, 533.4) * mm, "end": v(1171.28, -12.7) * mm});
            skLineSegment(sketch, "E39.right", {"start": v(-600.37, 533.4) * mm, "end": v(-600.37, -12.7) * mm});
            skSolve(sketch);
        }
        {
            var Q0;
            Q0 = qSketchRegion(id + "F63", true);
            extrude(context, id + "F64", {"entities" : qUnion([Q0]), "oppositeDirection" : true, "depth" : 6.35 * mm});
        }
    });
